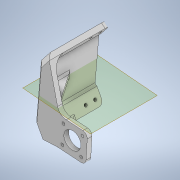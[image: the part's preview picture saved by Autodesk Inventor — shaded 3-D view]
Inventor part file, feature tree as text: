
AUTODESK INVENTOR PART (.ipt)
format: ipt  version: 2020 (Build 240168000, 168)  size: 354,304 bytes
history: native  units: mm
features: sketch x8, reference x8, projected_geometry x8, extrude x6, fillet x6, other x4, hole x2, plane x2, shell x2, chamfer x1
ambient origin geometry x8: Origin, YZ Plane, XZ Plane, XY Plane, X Axis, Y Axis, Z Axis, Center Point
bodies: Solid1 (feature_tree)
feature tree (47):
  extrude  "Extrusion1"  Depth=5.0mm
  hole  "Hole1"  [1 undecoded]
  hole  "Hole2"  [1 undecoded]
  extrude  "Extrusion2"  Depth=102.0mm
  sketch  "Sketch5"  dims[d13=3.0mm d14=6.0mm d15=4.0mm d16=2.0mm d17=90.0deg d18=8.0mm d19=20.594885mm d20=25.0mm d21=0.0mm]
  plane  "Work Plane1"
  extrude  "Extrusion3"  Depth=40.0mm
  extrude  "Extrusion4"  Depth=2.0mm
  plane  "Work Plane2"
  extrude  "Extrusion5"  Depth=30.0mm
  extrude  "Extrusion6"  Depth=30.0mm
  fillet  "Fillet1"  Radius=3.0mm
  fillet  "Fillet2"  Radius=3.0mm
  fillet  "Fillet3"  Radius=3.0mm
  fillet  "Fillet4"  Radius=3.0mm
  fillet  "Fillet5"  Radius=18.0mm
  fillet  "Fillet6"  Radius=5.0mm
  chamfer  "Chamfer1"  Distance=30.0mm
  sketch  "Sketch1"  dims[d0=5.0mm d1=5.0mm]
  reference  "Reference1"
  reference  "Reference2"
  sketch  "Sketch2"  dims[d2=5.0mm d3=5.0mm]
  reference  "Reference3"
  reference  "Reference4"
  sketch  "Sketch3"  dims[d4=25.0mm d5=0.0mm]
  reference  "Reference5"
  reference  "Reference6"
  sketch  "Sketch4"  dims[d6=3.0mm d7=6.0mm d8=4.0mm d9=2.0mm d10=90.0deg d11=8.0mm d12=20.594885mm]
  projected_geometry  "Projected Loop1"
  projected_geometry  "Projected Loop2"
  projected_geometry  "Projected Loop3"
  sketch  "Sketch6"  dims[d22=25.0mm d23=0.0mm d24=102.0mm]
  reference  "Reference7"
  reference  "Reference8"
  projected_geometry  "Projected Loop4"
  sketch  "Sketch7"  dims[d25=20.0mm d26=40.0mm]
  projected_geometry  "Projected Loop5"
  projected_geometry  "Projected Loop6"
  sketch  "Sketch8"  dims[d27=20.0mm d28=20.0mm d29=30.0mm d30=30.0mm d31=3.0mm d32=3.0mm d33=3.0mm d34=3.0mm d35=18.0mm d36=5.0mm d37=0.0mm d38=30.0mm d39=20.0mm d40=5.0mm d41=0.0mm d42=30.0mm d43=15.0mm d44=3.0mm d45=0.0mm d46=10.0mm d47=2.0mm d48=2.0mm d49=10.0mm d50=5.0mm d51=5.0mm d52=5.0mm d53=2.0mm d54=45.0deg]
  projected_geometry  "Projected Loop7"
  projected_geometry  "Projected Loop8"
  parser-record x1  (decoder bookkeeping rows leaked as tree rows — omitted from the tree; the rows remain in map.json)
  other  "reducer_2.iam"
  shell  "shell_2:3"  Thickness=20.0mm
  shell  "shell_2:4"  Thickness=5.0mm
  other  "bearing_8_16_5:3"
  other  "bearing_8_16_5:1"
note: 2 required parameter values undecoded (feature->parameter linkage not recoverable at this tier; creation-order binding heuristic only, values carry confidence <= 0.55)
note: 1 file-system path scrubbed to <path> (originals preserved in map.json)
